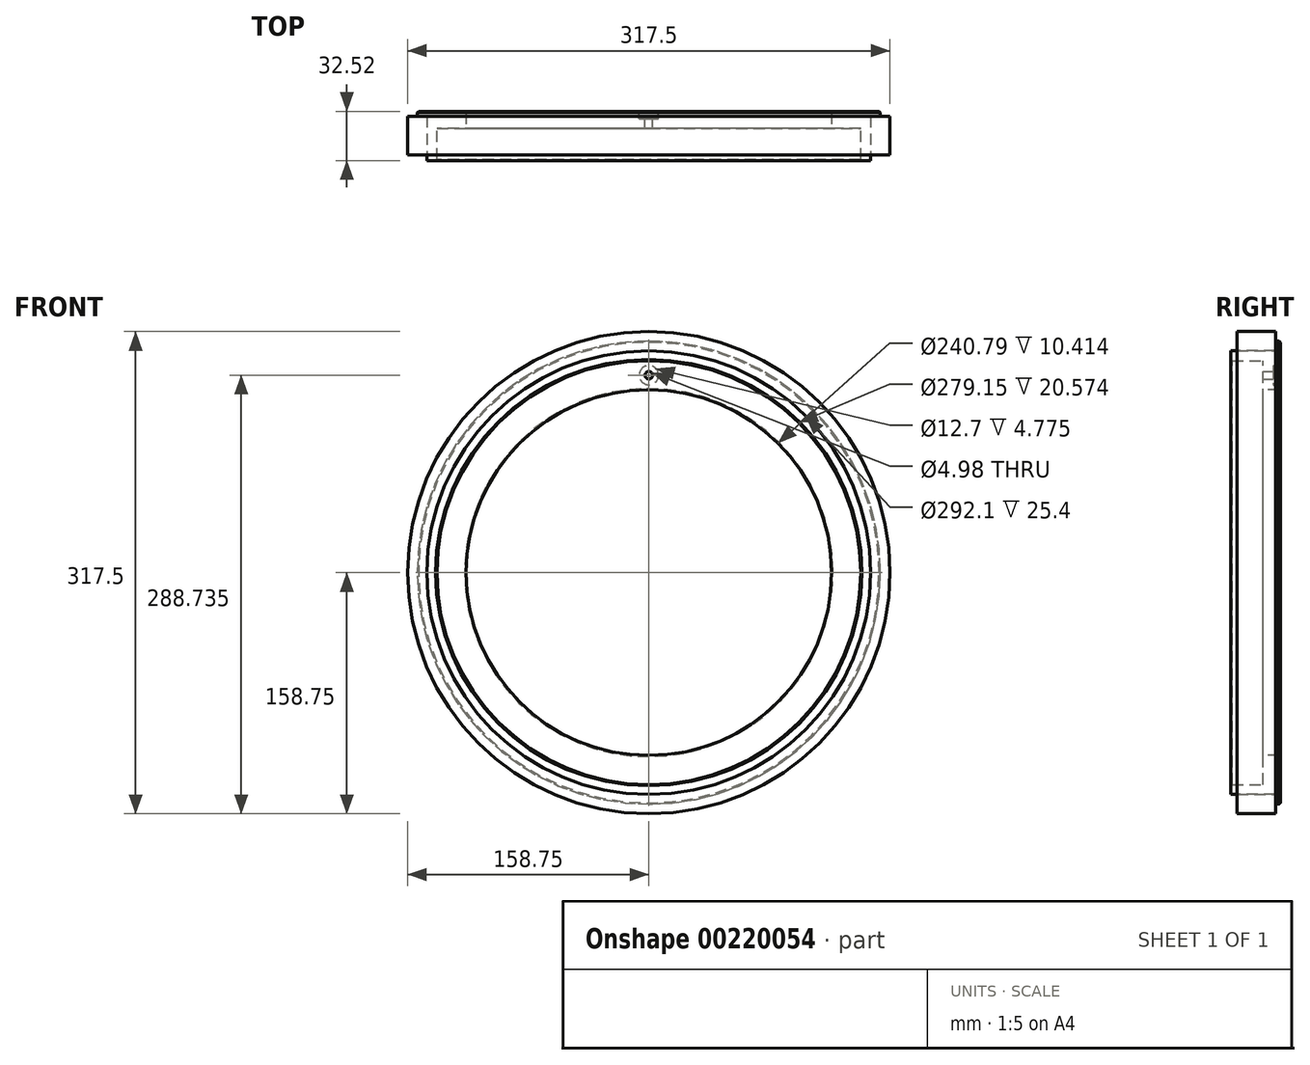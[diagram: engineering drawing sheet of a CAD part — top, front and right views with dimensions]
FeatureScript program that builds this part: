
annotation { "Feature Type Name" : "Feature", "Feature Type Description" : "" }
export const myFeature = defineFeature(function(context is Context, id is Id, definition is map)
    precondition{}
    {
        {
            var Q0;
            Q0=qCreatedBy(makeId("Front.planeOp"),FACE);
            var sketch = newSketch(context, id + "F0", { "sketchPlane" : qUnion([Q0])});
            skCircle(sketch, "E0", {"center": v(0, 0) * mm, "radius": 139.45 * mm, "construction": true});
            skCircle(sketch, "E1", {"center": v(0, 0) * mm, "radius": 120.4 * mm});
            skCircle(sketch, "E2", {"center": v(0, 0) * mm, "radius": 152.4 * mm});
            skSolve(sketch);
        }
        {
            var Q0;
            Q0 = qSketchRegion(id + "F0", true);
            extrude(context, id + "F1", {"entities" : qUnion([Q0]), "oppositeDirection" : true, "depth" : 11.18 * mm});
        }
        {
            var Q0;
            Q0=makeQuery(id+"F1.opExtrude","CAP_FACE",FACE,{"disambiguationData":[OSD([sQuery(id+"F0.wireOp",EDGE,"E1"),sQuery(id+"F0.wireOp",EDGE,"E2")])],"isStart":true});
            var sketch = newSketch(context, id + "F2", { "sketchPlane" : qUnion([Q0])});
            skCircle(sketch, "E3", {"center": v(0, 0) * mm, "radius": 139.57 * mm});
            skCircle(sketch, "E4.0", {"center": v(0, 0) * mm, "radius": 152.4 * mm});
            skSolve(sketch);
        }
        {
            var Q0;
            Q0 = qSketchRegion(id + "F2", true);
            extrude(context, id + "F3", {"entities" : qUnion([Q0]), "operationType" : NewBodyOperationType.ADD, "depth" : 21.34 * mm});
        }
        {
            var Q0;
            Q0=qCreatedBy(makeId("Top.planeOp"),FACE);
            var sketch = newSketch(context, id + "F4", { "sketchPlane" : qUnion([Q0])});
            skLineSegment(sketch, "E5", {"start": v(152.4, -21.34) * mm, "end": v(152.4, 11.18) * mm, "construction": true});
            skLineSegment(sketch, "E6", {"start": v(0, 0) * mm, "end": v(0, -20.34) * mm, "construction": true});
            skLineSegment(sketch, "E7", {"start": v(176, 8) * mm, "end": v(146.05, 8) * mm});
            skLineSegment(sketch, "E8", {"start": v(146.05, 8) * mm, "end": v(146.05, -18.16) * mm});
            skLineSegment(sketch, "E9", {"start": v(146.05, -18.16) * mm, "end": v(176, -18.16) * mm, "construction": true});
            skLineSegment(sketch, "E10", {"start": v(176, -18.16) * mm, "end": v(176, 8) * mm});
            skPoint(sketch, "E11.end.orphan", {"position": v(-152.4, -21.34) * mm});
            skPoint(sketch, "E11.start.orphan", {"position": v(-152.4, 11.18) * mm});
            skLineSegment(sketch, "E12", {"start": v(152.4, -21.34) * mm, "end": v(146.05, -21.34) * mm});
            skLineSegment(sketch, "E13", {"start": v(152.4, -21.34) * mm, "end": v(176, -21.34) * mm});
            skLineSegment(sketch, "E14", {"start": v(176, -18.16) * mm, "end": v(176, -21.34) * mm});
            skLineSegment(sketch, "E15", {"start": v(146.05, -18.16) * mm, "end": v(146.05, -21.34) * mm});
            skPoint(sketch, "E16.orphan", {"position": v(190.2, -21.34) * mm});
            skSolve(sketch);
        }
        {
            var Q0;
            Q0 = qSketchRegion(id + "F4", true);
            var Q1;
            Q1=sQuery(id+"F4.wireOp",EDGE,"E6");
            revolve(context, id + "F5", {"operationType" : NewBodyOperationType.REMOVE, "entities" : qUnion([Q0]), "axis" : qUnion([Q1]), "revolveType" : RevolveType.FULL, "oppositeDirection" : true});
        }
        {
            var Q0;
            Q0=makeQuery(id+"F1.opExtrude","CAP_EDGE",EDGE,{"disambiguationData":[OSD([sQuery(id+"F0.wireOp",EDGE,"E1")])],"isStart":false});
            var Q1;
            Q1=makeQuery(id+"F1.opExtrude","CAP_EDGE",EDGE,{"disambiguationData":[OSD([sQuery(id+"F0.wireOp",EDGE,"E2")])],"isStart":false});
            var Q2;
            Q2=makeQuery(id+"F3.opExtrude","CAP_EDGE",EDGE,{"disambiguationData":[OSD([sQuery(id+"F2.wireOp",EDGE,"E4.0")])],"isStart":false});
            var Q3;
            Q3=makeQuery(id+"F3.opExtrude","CAP_EDGE",EDGE,{"disambiguationData":[OSD([sQuery(id+"F2.wireOp",EDGE,"E3")])],"isStart":false});
            var Q4;
            Q4=makeQuery(id+"F5.boolean.opBoolean","COPY",EDGE,{"derivedFrom":makeQuery(id+"F5.opRevolve","SWEPT_EDGE",EDGE,{"disambiguationData":[OSD([sQuery(id+"F4.wireOp",EDGE,"E12"),sQuery(id+"F4.wireOp",EDGE,"E15")])]})});
            chamfer(context, id + "F6", {"entities" : qUnion([Q0, Q1, Q2, Q3, Q4]), "width" : 0.76 * mm, "tangentPropagation" : true});
        }
        {
            var Q0;
            Q0=qCreatedBy(makeId("Top.planeOp"),FACE);
            var sketch = newSketch(context, id + "F7", { "sketchPlane" : qUnion([Q0])});
            skLineSegment(sketch, "E17", {"start": v(146.05, 8) * mm, "end": v(146.05, 8) * mm});
            skLineSegment(sketch, "E18", {"start": v(-146.05, 8) * mm, "end": v(-146.05, 8) * mm});
            skLineSegment(sketch, "E19", {"start": v(146.05, 8) * mm, "end": v(158.75, 8) * mm});
            skLineSegment(sketch, "E20", {"start": v(158.75, 8) * mm, "end": v(158.75, 8) * mm});
            skLineSegment(sketch, "E21", {"start": v(0, 0) * mm, "end": v(0, -27.86) * mm, "construction": true});
            skLineSegment(sketch, "E22", {"start": v(146.05, 8) * mm, "end": v(146.05, -17.4) * mm});
            skLineSegment(sketch, "E23", {"start": v(146.05, -17.4) * mm, "end": v(158.75, -17.4) * mm});
            skLineSegment(sketch, "E24", {"start": v(158.75, 8) * mm, "end": v(158.75, -17.4) * mm});
            skSolve(sketch);
        }
        {
            var Q0;
            Q0 = qSketchRegion(id + "F7", true);
            var Q1;
            Q1=sQuery(id+"F7.wireOp",EDGE,"E21");
            revolve(context, id + "F8", {"entities" : qUnion([Q0]), "axis" : qUnion([Q1]), "revolveType" : RevolveType.FULL});
        }
        {
            var Q0;
            Q0=makeQuery(id+"F1.opExtrude","CAP_FACE",FACE,{"disambiguationData":[OSD([sQuery(id+"F0.wireOp",EDGE,"E1"),sQuery(id+"F0.wireOp",EDGE,"E2")])],"isStart":false});
            var sketch = newSketch(context, id + "F9", { "sketchPlane" : qUnion([Q0])});
            skLineSegment(sketch, "E25", {"start": v(0, 120.4) * mm, "end": v(0, 139.57) * mm, "construction": true});
            skCircle(sketch, "E26.0", {"center": v(0, 0) * mm, "radius": 120.4 * mm, "construction": true});
            skCircle(sketch, "E27.0", {"center": v(0, 0) * mm, "radius": 139.57 * mm, "construction": true});
            skCircle(sketch, "E28", {"center": v(0, 129.98) * mm, "radius": 6.35 * mm});
            skSolve(sketch);
        }
        {
            var Q0;
            Q0 = qSketchRegion(id + "F9", true);
            extrude(context, id + "F10", {"entities" : qUnion([Q0]), "operationType" : NewBodyOperationType.REMOVE, "oppositeDirection" : true, "depth" : 4.78 * mm});
        }
        {
            var Q0;
            Q0=makeQuery(id+"F1.opExtrude","CAP_FACE",FACE,{"disambiguationData":[OSD([sQuery(id+"F0.wireOp",EDGE,"E1"),sQuery(id+"F0.wireOp",EDGE,"E2")])],"isStart":false});
            var sketch = newSketch(context, id + "F11", { "sketchPlane" : qUnion([Q0])});
            skCircle(sketch, "E29.0", {"center": v(0, 129.98) * mm, "radius": 6.35 * mm, "construction": true});
            skCircle(sketch, "E30", {"center": v(0, 129.98) * mm, "radius": 2.49 * mm});
            skSolve(sketch);
        }
        {
            var Q0;
            Q0 = qSketchRegion(id + "F11", true);
            extrude(context, id + "F12", {"entities" : qUnion([Q0]), "operationType" : NewBodyOperationType.REMOVE, "oppositeDirection" : true, "depth" : 25.4 * mm});
        }
    });
